# Revit family: Screen-Beam_Mounted-Teknion-JNSASB-Solid_Add-On-R2018
name_source: partatom
category: Furniture
revit_build: Autodesk Revit 2018 (Build: 20190510_1515(x64)
units: mm (PartAtom-declared; Revit-internal decimal feet)

## family parameters
Always vertical = Yes
Cut with Voids When Loaded = No
OmniClass Number = 23.40.20.00
OmniClass Title = General Furniture and Specialties
Room Calculation Point = No
Shared = Yes
Work Plane-Based = No

## types (6) — shared parameters
Assembly Code = E2020200
Manufacturer = Teknion
Manufacturer Fax = 416.661.4586
Part Number = JNSASB
Product Documentation Link = http://www.teknion.com
Product Documentation Link 2 = https://www.teknion.com
Product Documentation Link 3 = https://www.teknion.com
Product Documentation Link 4 = https://www.teknion.com
Product Line = Expansion Cityline
Product Page URL = http://www.teknion.com
Series = Expansion Cityline
Sustainability Data = http://www.teknion.com
URL = www.teknion.com
Unit Weight URL = http://www.teknion.com
Warranty = http://www.teknion.com

## per-type parameters (varying)
| type | 120 Connection | Beam - Full | Beam - Half | Description | Height | Left Plane Offset | Low Height (18) | Model | Right Plane Offset | Standard Height (28) | Standard Width |
| Low Height (18), Standard Width | No | No | No | Solid Add-On Screen – Beam-Mounted, Low height (18 inches), 120 Connection Width Reduction for Lateral Application, Standard Corner Detail | 18 " | 0 " | Yes | JNSASBL____YS_ | 0 " | No | Yes |
| Low Height (18), 120 Connection | Yes | No | No | Solid Add-On Screen – Beam-Mounted, Low height (18 inches), 120 Connection Width Reduction for Lateral Application, Standard Corner Detail | 18 " | 0.489 " | Yes | JNSASBL____YS_ | 0.489 " | No | No |
| Standard Height (28), Standard Width | No | No | No | Solid Add-On Screen – Beam-Mounted, Standard Height (28 inches), Standard Width, Standard Corner Detail | 28.185 " | 0 " | No | JNSASBC____SS_ | 0 " | Yes | Yes |
| Standard Height (28), Beam - Half | No | No | Yes | Solid Add-On Screen – Beam-Mounted, Standard Height (28 inches), Beam - Half Width Reduction for Lateral Application, Standard Corner Detail | 28.185 " | 0.846 " | No | JNSASBC____AS_ | 0.846 " | Yes | No |
| Standard Height (28), Beam - Full | No | Yes | No | Solid Add-On Screen – Beam-Mounted, Standard Height (28 inches), Beam - Full Width Reduction for Lateral Application, Standard Corner Detail | 28.185 " | 1.693 " | No | JNSASBC____BS_ | 1.693 " | Yes | No |
| Standard Height (28), 120 Connection | Yes | No | No | Solid Add-On Screen – Beam-Mounted, Standard Height (28 inches),120 Connection Width Reduction for Lateral Application, Standard Corner Detail | 28.185 " | 0.489 " | No | JNSASBC____BS_ | 0.489 " | Yes | No |

## geometry (parser evidence)
native form markers: Sweep x3
no freeform markers — native parametric forms only
